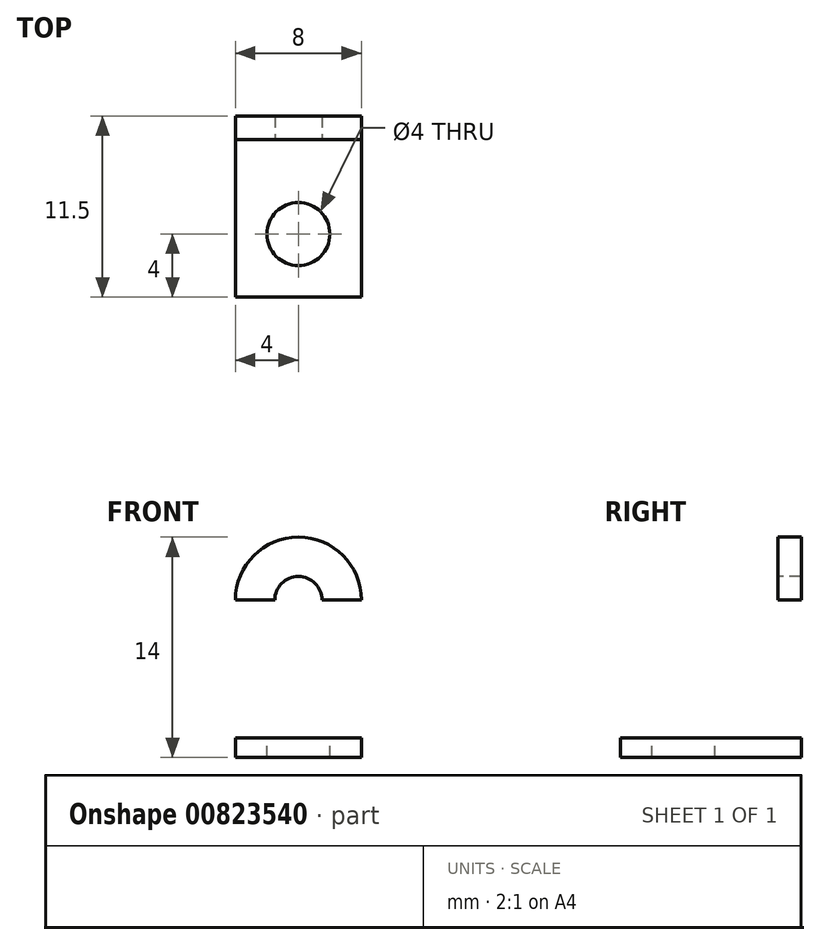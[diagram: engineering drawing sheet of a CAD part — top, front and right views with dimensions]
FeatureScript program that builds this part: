
annotation { "Feature Type Name" : "Feature", "Feature Type Description" : "" }
export const myFeature = defineFeature(function(context is Context, id is Id, definition is map)
    precondition{}
    {
        {
            var Q0;
            Q0=qCreatedBy(makeId("Front.planeOp"),FACE);
            var sketch = newSketch(context, id + "F0", { "sketchPlane" : qUnion([Q0])});
            skLineSegment(sketch, "E0.bottom", {"start": v(-4, 5) * mm, "end": v(4, 5) * mm});
            skLineSegment(sketch, "E0.top", {"start": v(-4, -5) * mm, "end": v(4, -5) * mm});
            skLineSegment(sketch, "E0.left", {"start": v(-4, 5) * mm, "end": v(-4, -5) * mm});
            skLineSegment(sketch, "E0.right", {"start": v(4, 5) * mm, "end": v(4, -5) * mm});
            skPoint(sketch, "E0.middle", {"position": v(0, 0) * mm});
            skArc(sketch, "E1", {"start": v(4, 5) * mm, "mid": v(0, 9) * mm, "end": v(-4, 5) * mm});
            skCircle(sketch, "E2", {"center": v(0, 5) * mm, "radius": 1.5 * mm});
            skLineSegment(sketch, "E3.top", {"start": v(-4, -3.75) * mm, "end": v(4, -3.75) * mm});
            skLineSegment(sketch, "E3.left", {"start": v(-4, -5) * mm, "end": v(-4, -3.75) * mm});
            skLineSegment(sketch, "E3.right", {"start": v(4, -5) * mm, "end": v(4, -3.75) * mm});
            skSolve(sketch);
        }
        {
            var Q0;
            {var subQ1=sQuery(id+"F0.wireOp",EDGE,"E0.left");Q0=makeQuery(id+"F0.imprint","IMPRINT",FACE,{"disambiguationData":[TD([[makeQuery(id+"F0.imprint","IMPRINT",EDGE,{"derivedFrom":subQ1}),1.0]])]});}
            var Q1;
            Q1=makeQuery(id+"F0.imprint","IMPRINT",FACE,{"disambiguationData":[TD([[makeQuery(id+"F0.imprint","IMPRINT",EDGE,{"derivedFrom":sQuery(id+"F0.wireOp",EDGE,"E0.top")}),1.0]])]});
            var Q2;
            {var subQ0=sQuery(id+"F0.wireOp",EDGE,"E1");Q2=makeQuery(id+"F0.imprint","IMPRINT",FACE,{"disambiguationData":[TD([[makeQuery(id+"F0.imprint","IMPRINT",EDGE,{"derivedFrom":subQ0}),1.0]])]});}
            extrude(context, id + "F1", {"entities" : qUnion([Q0, Q1, Q2]), "oppositeDirection" : true, "depth" : 1.5 * mm, "offsetDistance" : 25 * mm});
        }
        {
            var Q0;
            Q0=makeQuery(id+"F0.imprint","IMPRINT",FACE,{"disambiguationData":[TD([[makeQuery(id+"F0.imprint","IMPRINT",EDGE,{"derivedFrom":sQuery(id+"F0.wireOp",EDGE,"E0.top")}),1.0]])]});
            extrude(context, id + "F2", {"entities" : qUnion([Q0]), "operationType" : NewBodyOperationType.ADD, "depth" : 10 * mm, "offsetDistance" : 25 * mm});
        }
        {
            var Q0;
            Q0=makeQuery(id+"F2.opExtrude","SWEPT_FACE",FACE,{"disambiguationData":[OSD([sQuery(id+"F0.wireOp",EDGE,"E3.top")])]});
            var sketch = newSketch(context, id + "F3", { "sketchPlane" : qUnion([Q0])});
            skCircle(sketch, "E4", {"center": v(0, -6) * mm, "radius": 2 * mm});
            skLineSegment(sketch, "E5.bottom", {"start": v(-4, -10) * mm, "end": v(4, -10) * mm});
            skLineSegment(sketch, "E5.top", {"start": v(-4, -2) * mm, "end": v(4, -2) * mm});
            skLineSegment(sketch, "E5.left", {"start": v(-4, -10) * mm, "end": v(-4, -2) * mm});
            skLineSegment(sketch, "E5.right", {"start": v(4, -10) * mm, "end": v(4, -2) * mm});
            skLineSegment(sketch, "E6", {"start": v(-4, -2) * mm, "end": v(4, -10) * mm});
            skSolve(sketch);
        }
        {
            var Q0;
            {var subQ0=sQuery(id+"F3.wireOp",EDGE,"E6");var subQ1=sQuery(id+"F3.wireOp",EDGE,"E4");var subQ2=makeQuery(id+"F3.imprint","INTERSECT",VERTEX,{"disambiguationData":[OD(0.0)],"derivedFrom":[subQ1,subQ0]});Q0=makeQuery(id+"F3.imprint","IMPRINT",FACE,{"disambiguationData":[TD([[makeQuery(id+"F3.imprint","IMPRINT",EDGE,{"disambiguationData":[TD([[subQ2,1.0]])],"derivedFrom":subQ1}),1.0]])]});}
            var Q1;
            {var subQ0=sQuery(id+"F3.wireOp",EDGE,"E6");var subQ1=sQuery(id+"F3.wireOp",EDGE,"E4");var subQ2=makeQuery(id+"F3.imprint","INTERSECT",VERTEX,{"disambiguationData":[OD(0.0)],"derivedFrom":[subQ1,subQ0]});Q1=makeQuery(id+"F3.imprint","IMPRINT",FACE,{"disambiguationData":[TD([[makeQuery(id+"F3.imprint","IMPRINT",EDGE,{"disambiguationData":[TD([[subQ2,-1.0]])],"derivedFrom":subQ1}),1.0]])]});}
            extrude(context, id + "F4", {"entities" : qUnion([Q0, Q1]), "operationType" : NewBodyOperationType.REMOVE, "endBound" : BoundingType.UP_TO_NEXT, "oppositeDirection" : true, "depth" : 25 * mm, "offsetDistance" : 25 * mm});
        }
    });
